# Revit family: Haworth_JiveTable_Rectangle_Legs
name_source: partatom
category: Furniture Systems
revit_build: Autodesk Revit 2018 (Build: 20170223_1515(x64)
units: mm (PartAtom-declared; Revit-internal decimal feet)

## family parameters
Always vertical = Yes
Cut with Voids When Loaded = No
OmniClass Number = 23.40.70.14.64.21
OmniClass Title = Systems Furniture
Part Type = Normal
Room Calculation Point = No
Round Connector Dimension = Use Diameter
Shared = No
Work Plane-Based = No

## types (268) — shared parameters
Assembly Code = E2020200
Custom Size = No
Leg Length = 14 141/256"
Manufacturer = Haworth, Inc.
Max. Depth = 60"
Max. Height = 42"
Max. Width = 84"
Min. Depth = 18"
Min. Height = 16"
Min. Width = 24"
Model = Hawoth Jive
Revision Number = 0
Size = Verify Final Dim. w/ Haworth
Standard Depths = 18, 24, 30, 36, 42, 48, 54, 60 in.
Standard Height = 16, 20, 29, 36, 42 in.
Standard Widths = 24, 30, 36, 42, 48, 54, 60, 66, 72, 84 in.
Table Thickness = 1 3/16"
URL = http://www.haworth.com
URL - Product = http://www.haworth.com
Warranty = http://www.haworth.com

## per-type parameters (varying)
| type | Actual Casters | Actual Depth | Actual Height | Actual Width | C Leg Extruded | C Leg Round | Casters | Depth | Description | Glides | Height | Leg Distance | Leg Height | Leg Spacing | Post Extruded Leg | Post Leg Spacing | Post Round Leg | T Leg Extruded | T Leg Round | Width |
| 30d 30w 29h - Post Extruded Base - With Casters | Yes | 30" | 29" | 30" | No | No | Yes | 30" | Haworth Jive Table Square Legs - 30d 30w 29h - Post Extruded Base - With Casters | No | 29" | 4 1/256" | 27 13/16" | 10 255/256" | Yes | 21 127/128" | No | No | No | 30" |
| 36d 36w 29h - Post Extruded Base - With Casters | Yes | 36" | 29" | 36" | No | No | Yes | 36" | Haworth Jive Table Square Legs - 36d 36w 29h - Post Extruded Base - With Casters | No | 29" | 4 1/256" | 27 13/16" | 13 255/256" | Yes | 27 127/128" | No | No | No | 36" |
| 42d 42w 29h - Post Extruded Base - With Casters | Yes | 42" | 29" | 42" | No | No | Yes | 42" | Haworth Jive Table Square Legs - 42d 42w 29h - Post Extruded Base - With Casters | No | 29" | 4 1/256" | 27 13/16" | 16 255/256" | Yes | 33 127/128" | No | No | No | 42" |
| 48d 48w 29h - Post Extruded Base - With Casters | Yes | 48" | 29" | 48" | No | No | Yes | 48" | Haworth Jive Table Square Legs - 48d 48w 29h - Post Extruded Base - With Casters | No | 29" | 4 1/256" | 27 13/16" | 19 255/256" | Yes | 39 127/128" | No | No | No | 48" |
| 54d 54w 29h - Post Extruded Base - With Casters | Yes | 54" | 29" | 54" | No | No | Yes | 54" | Haworth Jive Table Square Legs - 54d 54w 29h - Post Extruded Base - With Casters | No | 29" | 4 1/256" | 27 13/16" | 22 255/256" | Yes | 45 127/128" | No | No | No | 54" |
| 60d 60w 29h - Post Extruded Base - With Casters | Yes | 60" | 29" | 60" | No | No | Yes | 60" | Haworth Jive Table Square Legs - 60d 60w 29h - Post Extruded Base - With Casters | No | 29" | 4 1/256" | 27 13/16" | 25 255/256" | Yes | 51 127/128" | No | No | No | 60" |
| 24d 24w 16h - Post Extruded Base - With Glides | No | 24" | 16" | 24" | No | No | No | 24" | Haworth Jive Table Square Legs - 24d 24w 16h - Post Extruded Base - With Glides | Yes | 16" | 4 1/256" | 14 13/16" | 7 255/256" | Yes | 15 127/128" | No | No | No | 24" |
| 36d 36w 16h - Post Extruded Base - With Glides | No | 36" | 16" | 36" | No | No | No | 36" | Haworth Jive Table Square Legs - 36d 36w 16h - Post Extruded Base - With Glides | Yes | 16" | 4 1/256" | 14 13/16" | 13 255/256" | Yes | 27 127/128" | No | No | No | 36" |
| 42d 42w 16h - Post Extruded Base - With Glides | No | 42" | 16" | 42" | No | No | No | 42" | Haworth Jive Table Square Legs - 42d 42w 16h - Post Extruded Base - With Glides | Yes | 16" | 4 1/256" | 14 13/16" | 16 255/256" | Yes | 33 127/128" | No | No | No | 42" |
| 48d 48w 16h - Post Extruded Base - With Glides | No | 48" | 16" | 48" | No | No | No | 48" | Haworth Jive Table Square Legs - 48d 48w 16h - Post Extruded Base - With Glides | Yes | 16" | 4 1/256" | 14 13/16" | 19 255/256" | Yes | 39 127/128" | No | No | No | 48" |
| 24d 24w 20h - Post Extruded Base - With Glides | No | 24" | 20" | 24" | No | No | No | 24" | Haworth Jive Table Square Legs - 24d 24w 20h - Post Extruded Base - With Glides | Yes | 20" | 4 1/256" | 18 13/16" | 7 255/256" | Yes | 15 127/128" | No | No | No | 24" |
| 36d 36w 20h - Post Extruded Base - With Glides | No | 36" | 20" | 36" | No | No | No | 36" | Haworth Jive Table Square Legs - 36d 36w 20h - Post Extruded Base - With Glides | Yes | 20" | 4 1/256" | 18 13/16" | 13 255/256" | Yes | 27 127/128" | No | No | No | 36" |
| 42d 42w 20h - Post Extruded Base - With Glides | No | 42" | 20" | 42" | No | No | No | 42" | Haworth Jive Table Square Legs - 42d 42w 20h - Post Extruded Base - With Glides | Yes | 20" | 4 1/256" | 18 13/16" | 16 255/256" | Yes | 33 127/128" | No | No | No | 42" |
| 48d 48w 20h - Post Extruded Base - With Glides | No | 48" | 20" | 48" | No | No | No | 48" | Haworth Jive Table Square Legs - 48d 48w 20h - Post Extruded Base - With Glides | Yes | 20" | 4 1/256" | 18 13/16" | 19 255/256" | Yes | 39 127/128" | No | No | No | 48" |
| 30d 30w 29h - Post Extruded Base - With Glides | No | 30" | 29" | 30" | No | No | No | 30" | Haworth Jive Table Square Legs - 30d 30w 29h - Post Extruded Base - With Glides | Yes | 29" | 4 1/256" | 27 13/16" | 10 255/256" | Yes | 21 127/128" | No | No | No | 30" |
| 36d 36w 29h - Post Extruded Base - With Glides | No | 36" | 29" | 36" | No | No | No | 36" | Haworth Jive Table Square Legs - 36d 36w 29h - Post Extruded Base - With Glides | Yes | 29" | 4 1/256" | 27 13/16" | 13 255/256" | Yes | 27 127/128" | No | No | No | 36" |
| 42d 42w 29h - Post Extruded Base - With Glides | No | 42" | 29" | 42" | No | No | No | 42" | Haworth Jive Table Square Legs - 42d 42w 29h - Post Extruded Base - With Glides | Yes | 29" | 4 1/256" | 27 13/16" | 16 255/256" | Yes | 33 127/128" | No | No | No | 42" |
| 48d 48w 29h - Post Extruded Base - With Glides | No | 48" | 29" | 48" | No | No | No | 48" | Haworth Jive Table Square Legs - 48d 48w 29h - Post Extruded Base - With Glides | Yes | 29" | 4 1/256" | 27 13/16" | 19 255/256" | Yes | 39 127/128" | No | No | No | 48" |
| 54d 54w 29h - Post Extruded Base - With Glides | No | 54" | 29" | 54" | No | No | No | 54" | Haworth Jive Table Square Legs - 54d 54w 29h - Post Extruded Base - With Glides | Yes | 29" | 4 1/256" | 27 13/16" | 22 255/256" | Yes | 45 127/128" | No | No | No | 54" |
| 60d 60w 29h - Post Extruded Base - With Glides | No | 60" | 29" | 60" | No | No | No | 60" | Haworth Jive Table Square Legs - 60d 60w 29h - Post Extruded Base - With Glides | Yes | 29" | 4 1/256" | 27 13/16" | 25 255/256" | Yes | 51 127/128" | No | No | No | 60" |
| 18d 48w 29h - Post Extruded Base - With Casters | Yes | 18" | 29" | 48" | No | No | Yes | 18" | Haworth Jive Table Rectangle Legs - 18d 48w 29h - Post Extruded Base - With Casters | No | 29" | 4 1/256" | 27 13/16" | 4 255/256" | Yes | 9 127/128" | No | No | No | 48" |
| 18d 54w 29h - Post Extruded Base - With Casters | Yes | 18" | 29" | 54" | No | No | Yes | 18" | Haworth Jive Table Rectangle Legs - 18d 54w 29h - Post Extruded Base - With Casters | No | 29" | 4 1/256" | 27 13/16" | 4 255/256" | Yes | 9 127/128" | No | No | No | 54" |
| 18d 60w 29h - Post Extruded Base - With Casters | Yes | 18" | 29" | 60" | No | No | Yes | 18" | Haworth Jive Table Rectangle Legs - 18d 60w 29h - Post Extruded Base - With Casters | No | 29" | 4 1/256" | 27 13/16" | 4 255/256" | Yes | 9 127/128" | No | No | No | 60" |
| 18d 66w 29h - Post Extruded Base - With Casters | Yes | 18" | 29" | 66" | No | No | Yes | 18" | Haworth Jive Table Rectangle Legs - 18d 66w 29h - Post Extruded Base - With Casters | No | 29" | 4 1/256" | 27 13/16" | 4 255/256" | Yes | 9 127/128" | No | No | No | 66" |
| 18d 72w 29h - Post Extruded Base - With Casters | Yes | 18" | 29" | 72" | No | No | Yes | 18" | Haworth Jive Table Rectangle Legs - 18d 72w 29h - Post Extruded Base - With Casters | No | 29" | 4 1/256" | 27 13/16" | 4 255/256" | Yes | 9 127/128" | No | No | No | 72" |
| 24d 36w 29h - Post Extruded Base - With Casters | Yes | 24" | 29" | 36" | No | No | Yes | 24" | Haworth Jive Table Rectangle Legs - 24d 36w 29h - Post Extruded Base - With Casters | No | 29" | 4 1/256" | 27 13/16" | 7 255/256" | Yes | 15 127/128" | No | No | No | 36" |
| 24d 42w 29h - Post Extruded Base - With Casters | Yes | 24" | 29" | 42" | No | No | Yes | 24" | Haworth Jive Table Rectangle Legs - 24d 42w 29h - Post Extruded Base - With Casters | No | 29" | 4 1/256" | 27 13/16" | 7 255/256" | Yes | 15 127/128" | No | No | No | 42" |
| 24d 48w 29h - Post Extruded Base - With Casters | Yes | 24" | 29" | 48" | No | No | Yes | 24" | Haworth Jive Table Rectangle Legs - 24d 48w 29h - Post Extruded Base - With Casters | No | 29" | 4 1/256" | 27 13/16" | 7 255/256" | Yes | 15 127/128" | No | No | No | 48" |
| 24d 54w 29h - Post Extruded Base - With Casters | Yes | 24" | 29" | 54" | No | No | Yes | 24" | Haworth Jive Table Rectangle Legs - 24d 54w 29h - Post Extruded Base - With Casters | No | 29" | 4 1/256" | 27 13/16" | 7 255/256" | Yes | 15 127/128" | No | No | No | 54" |
| 24d 60w 29h - Post Extruded Base - With Casters | Yes | 24" | 29" | 60" | No | No | Yes | 24" | Haworth Jive Table Rectangle Legs - 24d 60w 29h - Post Extruded Base - With Casters | No | 29" | 4 1/256" | 27 13/16" | 7 255/256" | Yes | 15 127/128" | No | No | No | 60" |
| 24d 66w 29h - Post Extruded Base - With Casters | Yes | 24" | 29" | 66" | No | No | Yes | 24" | Haworth Jive Table Rectangle Legs - 24d 66w 29h - Post Extruded Base - With Casters | No | 29" | 4 1/256" | 27 13/16" | 7 255/256" | Yes | 15 127/128" | No | No | No | 66" |
| 24d 72w 29h - Post Extruded Base - With Casters | Yes | 24" | 29" | 72" | No | No | Yes | 24" | Haworth Jive Table Rectangle Legs - 24d 72w 29h - Post Extruded Base - With Casters | No | 29" | 4 1/256" | 27 13/16" | 7 255/256" | Yes | 15 127/128" | No | No | No | 72" |
| 30d 36w 29h - Post Extruded Base - With Casters | Yes | 30" | 29" | 36" | No | No | Yes | 30" | Haworth Jive Table Rectangle Legs - 30d 36w 29h - Post Extruded Base - With Casters | No | 29" | 4 1/256" | 27 13/16" | 10 255/256" | Yes | 21 127/128" | No | No | No | 36" |
| 30d 42w 29h - Post Extruded Base - With Casters | Yes | 30" | 29" | 42" | No | No | Yes | 30" | Haworth Jive Table Rectangle Legs - 30d 42w 29h - Post Extruded Base - With Casters | No | 29" | 4 1/256" | 27 13/16" | 10 255/256" | Yes | 21 127/128" | No | No | No | 42" |
| 30d 48w 29h - Post Extruded Base - With Casters | Yes | 30" | 29" | 48" | No | No | Yes | 30" | Haworth Jive Table Rectangle Legs - 30d 48w 29h - Post Extruded Base - With Casters | No | 29" | 4 1/256" | 27 13/16" | 10 255/256" | Yes | 21 127/128" | No | No | No | 48" |
| 30d 60w 29h - Post Extruded Base - With Casters | Yes | 30" | 29" | 60" | No | No | Yes | 30" | Haworth Jive Table Rectangle Legs - 30d 60w 29h - Post Extruded Base - With Casters | No | 29" | 4 1/256" | 27 13/16" | 10 255/256" | Yes | 21 127/128" | No | No | No | 60" |
| 30d 72w 29h - Post Extruded Base - With Casters | Yes | 30" | 29" | 72" | No | No | Yes | 30" | Haworth Jive Table Rectangle Legs - 30d 72w 29h - Post Extruded Base - With Casters | No | 29" | 4 1/256" | 27 13/16" | 10 255/256" | Yes | 21 127/128" | No | No | No | 72" |
| 36d 60w 29h - Post Extruded Base - With Casters | Yes | 36" | 29" | 60" | No | No | Yes | 36" | Haworth Jive Table Rectangle Legs - 36d 60w 29h - Post Extruded Base - With Casters | No | 29" | 4 1/256" | 27 13/16" | 13 255/256" | Yes | 27 127/128" | No | No | No | 60" |
| 36d 66w 29h - Post Extruded Base - With Casters | Yes | 36" | 29" | 66" | No | No | Yes | 36" | Haworth Jive Table Rectangle Legs - 36d 66w 29h - Post Extruded Base - With Casters | No | 29" | 4 1/256" | 27 13/16" | 13 255/256" | Yes | 27 127/128" | No | No | No | 66" |
| 36d 72w 29h - Post Extruded Base - With Casters | Yes | 36" | 29" | 72" | No | No | Yes | 36" | Haworth Jive Table Rectangle Legs - 36d 72w 29h - Post Extruded Base - With Casters | No | 29" | 4 1/256" | 27 13/16" | 13 255/256" | Yes | 27 127/128" | No | No | No | 72" |
| 36d 84w 29h - Post Extruded Base - With Casters | Yes | 36" | 29" | 84" | No | No | Yes | 36" | Haworth Jive Table Rectangle Legs - 36d 84w 29h - Post Extruded Base - With Casters | No | 29" | 4 1/256" | 27 13/16" | 13 255/256" | Yes | 27 127/128" | No | No | No | 84" |
| 18d 48w 29h - Post Extruded Base - With Glides | No | 18" | 29" | 48" | No | No | No | 18" | Haworth Jive Table Rectangle Legs - 18d 48w 29h - Post Extruded Base - With Glides | Yes | 29" | 4 1/256" | 27 13/16" | 4 255/256" | Yes | 9 127/128" | No | No | No | 48" |
| 18d 54w 29h - Post Extruded Base - With Glides | No | 18" | 29" | 54" | No | No | No | 18" | Haworth Jive Table Rectangle Legs - 18d 54w 29h - Post Extruded Base - With Glides | Yes | 29" | 4 1/256" | 27 13/16" | 4 255/256" | Yes | 9 127/128" | No | No | No | 54" |
| 18d 60w 29h - Post Extruded Base - With Glides | No | 18" | 29" | 60" | No | No | No | 18" | Haworth Jive Table Rectangle Legs - 18d 60w 29h - Post Extruded Base - With Glides | Yes | 29" | 4 1/256" | 27 13/16" | 4 255/256" | Yes | 9 127/128" | No | No | No | 60" |
| 18d 66w 29h - Post Extruded Base - With Glides | No | 18" | 29" | 66" | No | No | No | 18" | Haworth Jive Table Rectangle Legs - 18d 66w 29h - Post Extruded Base - With Glides | Yes | 29" | 4 1/256" | 27 13/16" | 4 255/256" | Yes | 9 127/128" | No | No | No | 66" |
| 18d 72w 29h - Post Extruded Base - With Glides | No | 18" | 29" | 72" | No | No | No | 18" | Haworth Jive Table Rectangle Legs - 18d 72w 29h - Post Extruded Base - With Glides | Yes | 29" | 4 1/256" | 27 13/16" | 4 255/256" | Yes | 9 127/128" | No | No | No | 72" |
| 24d 36w 29h - Post Extruded Base - With Glides | No | 24" | 29" | 36" | No | No | No | 24" | Haworth Jive Table Rectangle Legs - 24d 36w 29h - Post Extruded Base - With Glides | Yes | 29" | 4 1/256" | 27 13/16" | 7 255/256" | Yes | 15 127/128" | No | No | No | 36" |
| 24d 42w 29h - Post Extruded Base - With Glides | No | 24" | 29" | 42" | No | No | No | 24" | Haworth Jive Table Rectangle Legs - 24d 42w 29h - Post Extruded Base - With Glides | Yes | 29" | 4 1/256" | 27 13/16" | 7 255/256" | Yes | 15 127/128" | No | No | No | 42" |
| 24d 48w 29h - Post Extruded Base - With Glides | No | 24" | 29" | 48" | No | No | No | 24" | Haworth Jive Table Rectangle Legs - 24d 48w 29h - Post Extruded Base - With Glides | Yes | 29" | 4 1/256" | 27 13/16" | 7 255/256" | Yes | 15 127/128" | No | No | No | 48" |
| 24d 54w 29h - Post Extruded Base - With Glides | No | 24" | 29" | 54" | No | No | No | 24" | Haworth Jive Table Rectangle Legs - 24d 54w 29h - Post Extruded Base - With Glides | Yes | 29" | 4 1/256" | 27 13/16" | 7 255/256" | Yes | 15 127/128" | No | No | No | 54" |
| 24d 60w 29h - Post Extruded Base - With Glides | No | 24" | 29" | 60" | No | No | No | 24" | Haworth Jive Table Rectangle Legs - 24d 60w 29h - Post Extruded Base - With Glides | Yes | 29" | 4 1/256" | 27 13/16" | 7 255/256" | Yes | 15 127/128" | No | No | No | 60" |
| 24d 66w 29h - Post Extruded Base - With Glides | No | 24" | 29" | 66" | No | No | No | 24" | Haworth Jive Table Rectangle Legs - 24d 66w 29h - Post Extruded Base - With Glides | Yes | 29" | 4 1/256" | 27 13/16" | 7 255/256" | Yes | 15 127/128" | No | No | No | 66" |
| 24d 72w 29h - Post Extruded Base - With Glides | No | 24" | 29" | 72" | No | No | No | 24" | Haworth Jive Table Rectangle Legs - 24d 72w 29h - Post Extruded Base - With Glides | Yes | 29" | 4 1/256" | 27 13/16" | 7 255/256" | Yes | 15 127/128" | No | No | No | 72" |
| 30d 36w 29h - Post Extruded Base - With Glides | No | 30" | 29" | 36" | No | No | No | 30" | Haworth Jive Table Rectangle Legs - 30d 36w 29h - Post Extruded Base - With Glides | Yes | 29" | 4 1/256" | 27 13/16" | 10 255/256" | Yes | 21 127/128" | No | No | No | 36" |
| 30d 42w 29h - Post Extruded Base - With Glides | No | 30" | 29" | 42" | No | No | No | 30" | Haworth Jive Table Rectangle Legs - 30d 42w 29h - Post Extruded Base - With Glides | Yes | 29" | 4 1/256" | 27 13/16" | 10 255/256" | Yes | 21 127/128" | No | No | No | 42" |
| 30d 48w 29h - Post Extruded Base - With Glides | No | 30" | 29" | 48" | No | No | No | 30" | Haworth Jive Table Rectangle Legs - 30d 48w 29h - Post Extruded Base - With Glides | Yes | 29" | 4 1/256" | 27 13/16" | 10 255/256" | Yes | 21 127/128" | No | No | No | 48" |
| 30d 60w 29h - Post Extruded Base - With Glides | No | 30" | 29" | 60" | No | No | No | 30" | Haworth Jive Table Rectangle Legs - 30d 60w 29h - Post Extruded Base - With Glides | Yes | 29" | 4 1/256" | 27 13/16" | 10 255/256" | Yes | 21 127/128" | No | No | No | 60" |
| 30d 72w 29h - Post Extruded Base - With Glides | No | 30" | 29" | 72" | No | No | No | 30" | Haworth Jive Table Rectangle Legs - 30d 72w 29h - Post Extruded Base - With Glides | Yes | 29" | 4 1/256" | 27 13/16" | 10 255/256" | Yes | 21 127/128" | No | No | No | 72" |
| 36d 60w 29h - Post Extruded Base - With Glides | No | 36" | 29" | 60" | No | No | No | 36" | Haworth Jive Table Rectangle Legs - 36d 60w 29h - Post Extruded Base - With Glides | Yes | 29" | 4 1/256" | 27 13/16" | 13 255/256" | Yes | 27 127/128" | No | No | No | 60" |
| 36d 66w 29h - Post Extruded Base - With Glides | No | 36" | 29" | 66" | No | No | No | 36" | Haworth Jive Table Rectangle Legs - 36d 66w 29h - Post Extruded Base - With Glides | Yes | 29" | 4 1/256" | 27 13/16" | 13 255/256" | Yes | 27 127/128" | No | No | No | 66" |
| 36d 72w 29h - Post Extruded Base - With Glides | No | 36" | 29" | 72" | No | No | No | 36" | Haworth Jive Table Rectangle Legs - 36d 72w 29h - Post Extruded Base - With Glides | Yes | 29" | 4 1/256" | 27 13/16" | 13 255/256" | Yes | 27 127/128" | No | No | No | 72" |
| 36d 84w 29h - Post Extruded Base - With Glides | No | 36" | 29" | 84" | No | No | No | 36" | Haworth Jive Table Rectangle Legs - 36d 84w 29h - Post Extruded Base - With Glides | Yes | 29" | 4 1/256" | 27 13/16" | 13 255/256" | Yes | 27 127/128" | No | No | No | 84" |
| 30d 30w 29h - Post Round Base - With Casters | Yes | 30" | 29" | 30" | No | No | Yes | 30" | Haworth Jive Table Square Legs - 30d 30w 29h - Post Round Base - With Casters | No | 29" | 4 1/256" | 27 13/16" | 10 255/256" | No | 21 127/128" | Yes | No | No | 30" |
| 36d 36w 29h - Post Round Base - With Casters | Yes | 36" | 29" | 36" | No | No | Yes | 36" | Haworth Jive Table Square Legs - 36d 36w 29h - Post Round Base - With Casters | No | 29" | 4 1/256" | 27 13/16" | 13 255/256" | No | 27 127/128" | Yes | No | No | 36" |
| 42d 42w 29h - Post Round Base - With Casters | Yes | 42" | 29" | 42" | No | No | Yes | 42" | Haworth Jive Table Square Legs - 42d 42w 29h - Post Round Base - With Casters | No | 29" | 4 1/256" | 27 13/16" | 16 255/256" | No | 33 127/128" | Yes | No | No | 42" |
| 48d 48w 29h - Post Round Base - With Casters | Yes | 48" | 29" | 48" | No | No | Yes | 48" | Haworth Jive Table Square Legs - 48d 48w 29h - Post Round Base - With Casters | No | 29" | 4 1/256" | 27 13/16" | 19 255/256" | No | 39 127/128" | Yes | No | No | 48" |
| 30d 30w 29h - Post Round Base - With Glides | No | 30" | 29" | 30" | No | No | No | 30" | Haworth Jive Table Square Legs - 30d 30w 29h - Post Round Base - With Glides | Yes | 29" | 4 1/256" | 27 13/16" | 10 255/256" | No | 21 127/128" | Yes | No | No | 30" |
| 36d 36w 29h - Post Round Base - With Glides | No | 36" | 29" | 36" | No | No | No | 36" | Haworth Jive Table Square Legs - 36d 36w 29h - Post Round Base - With Glides | Yes | 29" | 4 1/256" | 27 13/16" | 13 255/256" | No | 27 127/128" | Yes | No | No | 36" |
| 42d 42w 29h - Post Round Base - With Glides | No | 42" | 29" | 42" | No | No | No | 42" | Haworth Jive Table Square Legs - 42d 42w 29h - Post Round Base - With Glides | Yes | 29" | 4 1/256" | 27 13/16" | 16 255/256" | No | 33 127/128" | Yes | No | No | 42" |
| 48d 48w 29h - Post Round Base - With Glides | No | 48" | 29" | 48" | No | No | No | 48" | Haworth Jive Table Square Legs - 48d 48w 29h - Post Round Base - With Glides | Yes | 29" | 4 1/256" | 27 13/16" | 19 255/256" | No | 39 127/128" | Yes | No | No | 48" |
| 18d 48w 29h - Post Round Base - With Casters | Yes | 18" | 29" | 48" | No | No | Yes | 18" | Haworth Jive Table Rectangle Legs - 18d 48w 29h - Post Round Base - With Casters | No | 29" | 4 1/256" | 27 13/16" | 4 255/256" | No | 9 127/128" | Yes | No | No | 48" |
| 18d 54w 29h - Post Round Base - With Casters | Yes | 18" | 29" | 54" | No | No | Yes | 18" | Haworth Jive Table Rectangle Legs - 18d 54w 29h - Post Round Base - With Casters | No | 29" | 4 1/256" | 27 13/16" | 4 255/256" | No | 9 127/128" | Yes | No | No | 54" |
| 18d 60w 29h - Post Round Base - With Casters | Yes | 18" | 29" | 60" | No | No | Yes | 18" | Haworth Jive Table Rectangle Legs - 18d 60w 29h - Post Round Base - With Casters | No | 29" | 4 1/256" | 27 13/16" | 4 255/256" | No | 9 127/128" | Yes | No | No | 60" |
| 18d 66w 29h - Post Round Base - With Casters | Yes | 18" | 29" | 66" | No | No | Yes | 18" | Haworth Jive Table Rectangle Legs - 18d 66w 29h - Post Round Base - With Casters | No | 29" | 4 1/256" | 27 13/16" | 4 255/256" | No | 9 127/128" | Yes | No | No | 66" |
| 18d 72w 29h - Post Round Base - With Casters | Yes | 18" | 29" | 72" | No | No | Yes | 18" | Haworth Jive Table Rectangle Legs - 18d 72w 29h - Post Round Base - With Casters | No | 29" | 4 1/256" | 27 13/16" | 4 255/256" | No | 9 127/128" | Yes | No | No | 72" |
| 24d 36w 29h - Post Round Base - With Casters | Yes | 24" | 29" | 36" | No | No | Yes | 24" | Haworth Jive Table Rectangle Legs - 24d 36w 29h - Post Round Base - With Casters | No | 29" | 4 1/256" | 27 13/16" | 7 255/256" | No | 15 127/128" | Yes | No | No | 36" |
| 24d 42w 29h - Post Round Base - With Casters | Yes | 24" | 29" | 42" | No | No | Yes | 24" | Haworth Jive Table Rectangle Legs - 24d 42w 29h - Post Round Base - With Casters | No | 29" | 4 1/256" | 27 13/16" | 7 255/256" | No | 15 127/128" | Yes | No | No | 42" |
| 24d 48w 29h - Post Round Base - With Casters | Yes | 24" | 29" | 48" | No | No | Yes | 24" | Haworth Jive Table Rectangle Legs - 24d 48w 29h - Post Round Base - With Casters | No | 29" | 4 1/256" | 27 13/16" | 7 255/256" | No | 15 127/128" | Yes | No | No | 48" |
| 24d 54w 29h - Post Round Base - With Casters | Yes | 24" | 29" | 54" | No | No | Yes | 24" | Haworth Jive Table Rectangle Legs - 24d 54w 29h - Post Round Base - With Casters | No | 29" | 4 1/256" | 27 13/16" | 7 255/256" | No | 15 127/128" | Yes | No | No | 54" |
| 24d 60w 29h - Post Round Base - With Casters | Yes | 24" | 29" | 60" | No | No | Yes | 24" | Haworth Jive Table Rectangle Legs - 24d 60w 29h - Post Round Base - With Casters | No | 29" | 4 1/256" | 27 13/16" | 7 255/256" | No | 15 127/128" | Yes | No | No | 60" |
| 24d 66w 29h - Post Round Base - With Casters | Yes | 24" | 29" | 66" | No | No | Yes | 24" | Haworth Jive Table Rectangle Legs - 24d 66w 29h - Post Round Base - With Casters | No | 29" | 4 1/256" | 27 13/16" | 7 255/256" | No | 15 127/128" | Yes | No | No | 66" |
| 24d 72w 29h - Post Round Base - With Casters | Yes | 24" | 29" | 72" | No | No | Yes | 24" | Haworth Jive Table Rectangle Legs - 24d 72w 29h - Post Round Base - With Casters | No | 29" | 4 1/256" | 27 13/16" | 7 255/256" | No | 15 127/128" | Yes | No | No | 72" |
| 30d 36w 29h - Post Round Base - With Casters | Yes | 30" | 29" | 36" | No | No | Yes | 30" | Haworth Jive Table Rectangle Legs - 30d 36w 29h - Post Round Base - With Casters | No | 29" | 4 1/256" | 27 13/16" | 10 255/256" | No | 21 127/128" | Yes | No | No | 36" |
| 30d 42w 29h - Post Round Base - With Casters | Yes | 30" | 29" | 42" | No | No | Yes | 30" | Haworth Jive Table Rectangle Legs - 30d 42w 29h - Post Round Base - With Casters | No | 29" | 4 1/256" | 27 13/16" | 10 255/256" | No | 21 127/128" | Yes | No | No | 42" |
| 30d 48w 29h - Post Round Base - With Casters | Yes | 30" | 29" | 48" | No | No | Yes | 30" | Haworth Jive Table Rectangle Legs - 30d 48w 29h - Post Round Base - With Casters | No | 29" | 4 1/256" | 27 13/16" | 10 255/256" | No | 21 127/128" | Yes | No | No | 48" |
| 30d 54w 29h - Post Round Base - With Casters | Yes | 30" | 29" | 54" | No | No | Yes | 30" | Haworth Jive Table Rectangle Legs - 30d 54w 29h - Post Round Base - With Casters | No | 29" | 4 1/256" | 27 13/16" | 10 255/256" | No | 21 127/128" | Yes | No | No | 54" |
| 30d 60w 29h - Post Round Base - With Casters | Yes | 30" | 29" | 60" | No | No | Yes | 30" | Haworth Jive Table Rectangle Legs - 30d 60w 29h - Post Round Base - With Casters | No | 29" | 4 1/256" | 27 13/16" | 10 255/256" | No | 21 127/128" | Yes | No | No | 60" |
| 30d 72w 29h - Post Round Base - With Casters | Yes | 30" | 29" | 72" | No | No | Yes | 30" | Haworth Jive Table Rectangle Legs - 30d 72w 29h - Post Round Base - With Casters | No | 29" | 4 1/256" | 27 13/16" | 10 255/256" | No | 21 127/128" | Yes | No | No | 72" |
| 36d 60w 29h - Post Round Base - With Casters | Yes | 36" | 29" | 60" | No | No | Yes | 36" | Haworth Jive Table Rectangle Legs - 36d 60w 29h - Post Round Base - With Casters | No | 29" | 4 1/256" | 27 13/16" | 13 255/256" | No | 27 127/128" | Yes | No | No | 60" |
| 36d 66w 29h - Post Round Base - With Casters | Yes | 36" | 29" | 66" | No | No | Yes | 36" | Haworth Jive Table Rectangle Legs - 36d 66w 29h - Post Round Base - With Casters | No | 29" | 4 1/256" | 27 13/16" | 13 255/256" | No | 27 127/128" | Yes | No | No | 66" |
| 36d 72w 29h - Post Round Base - With Casters | Yes | 36" | 29" | 72" | No | No | Yes | 36" | Haworth Jive Table Rectangle Legs - 36d 72w 29h - Post Round Base - With Casters | No | 29" | 4 1/256" | 27 13/16" | 13 255/256" | No | 27 127/128" | Yes | No | No | 72" |
| 18d 48w 29h - Post Round Base - With Glides | No | 18" | 29" | 48" | No | No | No | 18" | Haworth Jive Table Rectangle Legs - 18d 48w 29h - Post Round Base - With Glides | Yes | 29" | 4 1/256" | 27 13/16" | 4 255/256" | No | 9 127/128" | Yes | No | No | 48" |
| 18d 54w 29h - Post Round Base - With Glides | No | 18" | 29" | 54" | No | No | No | 18" | Haworth Jive Table Rectangle Legs - 18d 54w 29h - Post Round Base - With Glides | Yes | 29" | 4 1/256" | 27 13/16" | 4 255/256" | No | 9 127/128" | Yes | No | No | 54" |
| 18d 60w 29h - Post Round Base - With Glides | No | 18" | 29" | 60" | No | No | No | 18" | Haworth Jive Table Rectangle Legs - 18d 60w 29h - Post Round Base - With Glides | Yes | 29" | 4 1/256" | 27 13/16" | 4 255/256" | No | 9 127/128" | Yes | No | No | 60" |
| 18d 66w 29h - Post Round Base - With Glides | No | 18" | 29" | 66" | No | No | No | 18" | Haworth Jive Table Rectangle Legs - 18d 66w 29h - Post Round Base - With Glides | Yes | 29" | 4 1/256" | 27 13/16" | 4 255/256" | No | 9 127/128" | Yes | No | No | 66" |
| 18d 72w 29h - Post Round Base - With Glides | No | 18" | 29" | 72" | No | No | No | 18" | Haworth Jive Table Rectangle Legs - 18d 72w 29h - Post Round Base - With Glides | Yes | 29" | 4 1/256" | 27 13/16" | 4 255/256" | No | 9 127/128" | Yes | No | No | 72" |
| 24d 36w 29h - Post Round Base - With Glides | No | 24" | 29" | 36" | No | No | No | 24" | Haworth Jive Table Rectangle Legs - 24d 36w 29h - Post Round Base - With Glides | Yes | 29" | 4 1/256" | 27 13/16" | 7 255/256" | No | 15 127/128" | Yes | No | No | 36" |
| 24d 42w 29h - Post Round Base - With Glides | No | 24" | 29" | 42" | No | No | No | 24" | Haworth Jive Table Rectangle Legs - 24d 42w 29h - Post Round Base - With Glides | Yes | 29" | 4 1/256" | 27 13/16" | 7 255/256" | No | 15 127/128" | Yes | No | No | 42" |
| 24d 48w 29h - Post Round Base - With Glides | No | 24" | 29" | 48" | No | No | No | 24" | Haworth Jive Table Rectangle Legs - 24d 48w 29h - Post Round Base - With Glides | Yes | 29" | 4 1/256" | 27 13/16" | 7 255/256" | No | 15 127/128" | Yes | No | No | 48" |
| 24d 54w 29h - Post Round Base - With Glides | No | 24" | 29" | 54" | No | No | No | 24" | Haworth Jive Table Rectangle Legs - 24d 54w 29h - Post Round Base - With Glides | Yes | 29" | 4 1/256" | 27 13/16" | 7 255/256" | No | 15 127/128" | Yes | No | No | 54" |
| 24d 60w 29h - Post Round Base - With Glides | No | 24" | 29" | 60" | No | No | No | 24" | Haworth Jive Table Rectangle Legs - 24d 60w 29h - Post Round Base - With Glides | Yes | 29" | 4 1/256" | 27 13/16" | 7 255/256" | No | 15 127/128" | Yes | No | No | 60" |
| 24d 66w 29h - Post Round Base - With Glides | No | 24" | 29" | 66" | No | No | No | 24" | Haworth Jive Table Rectangle Legs - 24d 66w 29h - Post Round Base - With Glides | Yes | 29" | 4 1/256" | 27 13/16" | 7 255/256" | No | 15 127/128" | Yes | No | No | 66" |
| 24d 72w 29h - Post Round Base - With Glides | No | 24" | 29" | 72" | No | No | No | 24" | Haworth Jive Table Rectangle Legs - 24d 72w 29h - Post Round Base - With Glides | Yes | 29" | 4 1/256" | 27 13/16" | 7 255/256" | No | 15 127/128" | Yes | No | No | 72" |
| 30d 36w 29h - Post Round Base - With Glides | No | 30" | 29" | 36" | No | No | No | 30" | Haworth Jive Table Rectangle Legs - 30d 36w 29h - Post Round Base - With Glides | Yes | 29" | 4 1/256" | 27 13/16" | 10 255/256" | No | 21 127/128" | Yes | No | No | 36" |
| 30d 42w 29h - Post Round Base - With Glides | No | 30" | 29" | 42" | No | No | No | 30" | Haworth Jive Table Rectangle Legs - 30d 42w 29h - Post Round Base - With Glides | Yes | 29" | 4 1/256" | 27 13/16" | 10 255/256" | No | 21 127/128" | Yes | No | No | 42" |
| 30d 48w 29h - Post Round Base - With Glides | No | 30" | 29" | 48" | No | No | No | 30" | Haworth Jive Table Rectangle Legs - 30d 48w 29h - Post Round Base - With Glides | Yes | 29" | 4 1/256" | 27 13/16" | 10 255/256" | No | 21 127/128" | Yes | No | No | 48" |
| 30d 54w 29h - Post Round Base - With Glides | No | 30" | 29" | 54" | No | No | No | 30" | Haworth Jive Table Rectangle Legs - 30d 54w 29h - Post Round Base - With Glides | Yes | 29" | 4 1/256" | 27 13/16" | 10 255/256" | No | 21 127/128" | Yes | No | No | 54" |
| 30d 60w 29h - Post Round Base - With Glides | No | 30" | 29" | 60" | No | No | No | 30" | Haworth Jive Table Rectangle Legs - 30d 60w 29h - Post Round Base - With Glides | Yes | 29" | 4 1/256" | 27 13/16" | 10 255/256" | No | 21 127/128" | Yes | No | No | 60" |
| 30d 72w 29h - Post Round Base - With Glides | No | 30" | 29" | 72" | No | No | No | 30" | Haworth Jive Table Rectangle Legs - 30d 72w 29h - Post Round Base - With Glides | Yes | 29" | 4 1/256" | 27 13/16" | 10 255/256" | No | 21 127/128" | Yes | No | No | 72" |
| 36d 60w 29h - Post Round Base - With Glides | No | 36" | 29" | 60" | No | No | No | 36" | Haworth Jive Table Rectangle Legs - 36d 60w 29h - Post Round Base - With Glides | Yes | 29" | 4 1/256" | 27 13/16" | 13 255/256" | No | 27 127/128" | Yes | No | No | 60" |
| 36d 66w 29h - Post Round Base - With Glides | No | 36" | 29" | 66" | No | No | No | 36" | Haworth Jive Table Rectangle Legs - 36d 66w 29h - Post Round Base - With Glides | Yes | 29" | 4 1/256" | 27 13/16" | 13 255/256" | No | 27 127/128" | Yes | No | No | 66" |
| 36d 72w 29h - Post Round Base - With Glides | No | 36" | 29" | 72" | No | No | No | 36" | Haworth Jive Table Rectangle Legs - 36d 72w 29h - Post Round Base - With Glides | Yes | 29" | 4 1/256" | 27 13/16" | 13 255/256" | No | 27 127/128" | Yes | No | No | 72" |
| 24d 36w 29h - C Leg Extruded - With Casters | Yes | 24" | 29" | 36" | Yes | No | Yes | 24" | Haworth Jive Table Rectangle Legs - 24d 36w 29h - C Leg Extruded - With Casters | No | 29" | 7 91/128" | 27 13/16" | 4 37/128" | No | 15 127/128" | No | No | No | 36" |
| 24d 42w 29h - C Leg Extruded - With Casters | Yes | 24" | 29" | 42" | Yes | No | Yes | 24" | Haworth Jive Table Rectangle Legs - 24d 42w 29h - C Leg Extruded - With Casters | No | 29" | 7 91/128" | 27 13/16" | 4 37/128" | No | 15 127/128" | No | No | No | 42" |
| 24d 48w 29h - C Leg Extruded - With Casters | Yes | 24" | 29" | 48" | Yes | No | Yes | 24" | Haworth Jive Table Rectangle Legs - 24d 48w 29h - C Leg Extruded - With Casters | No | 29" | 7 91/128" | 27 13/16" | 4 37/128" | No | 15 127/128" | No | No | No | 48" |
| 24d 54w 29h - C Leg Extruded- With Casters | Yes | 24" | 29" | 54" | Yes | No | Yes | 24" | Haworth Jive Table Rectangle Legs - 24d 54w 29h - C Leg Extruded- With Casters | No | 29" | 7 91/128" | 27 13/16" | 4 37/128" | No | 15 127/128" | No | No | No | 54" |
| 24d 60w 29h - C Leg Extruded - With Casters | Yes | 24" | 29" | 60" | Yes | No | Yes | 24" | Haworth Jive Table Rectangle Legs - 24d 60w 29h - C Leg Extruded - With Casters | No | 29" | 7 91/128" | 27 13/16" | 4 37/128" | No | 15 127/128" | No | No | No | 60" |
| 24d 66w 29h - C Leg Extruded - With Casters | Yes | 24" | 29" | 66" | Yes | No | Yes | 24" | Haworth Jive Table Rectangle Legs - 24d 66w 29h - C Leg Extruded - With Casters | No | 29" | 7 91/128" | 27 13/16" | 4 37/128" | No | 15 127/128" | No | No | No | 66" |
| 24d 72w 29h - C Leg Extruded - With Casters | Yes | 24" | 29" | 72" | Yes | No | Yes | 24" | Haworth Jive Table Rectangle Legs - 24d 72w 29h - C Leg Extruded - With Casters | No | 29" | 7 91/128" | 27 13/16" | 4 37/128" | No | 15 127/128" | No | No | No | 72" |
| 30d 36w 29h - C Leg Extruded - With Casters | Yes | 30" | 29" | 36" | Yes | No | Yes | 30" | Haworth Jive Table Rectangle Legs - 30d 36w 29h - C Leg Extruded - With Casters | No | 29" | 7 91/128" | 27 13/16" | 7 37/128" | No | 21 127/128" | No | No | No | 36" |
| 30d 42w 29h - C Leg Extruded - With Casters | Yes | 30" | 29" | 42" | Yes | No | Yes | 30" | Haworth Jive Table Rectangle Legs - 30d 42w 29h - C Leg Extruded - With Casters | No | 29" | 7 91/128" | 27 13/16" | 7 37/128" | No | 21 127/128" | No | No | No | 42" |
| 30d 48w 29h - C Leg Extruded - With Casters | Yes | 30" | 29" | 48" | Yes | No | Yes | 30" | Haworth Jive Table Rectangle Legs - 30d 48w 29h - C Leg Extruded - With Casters | No | 29" | 7 91/128" | 27 13/16" | 7 37/128" | No | 21 127/128" | No | No | No | 48" |
| 30d 54w 29h - C Leg Extruded - With Casters | Yes | 30" | 29" | 54" | Yes | No | Yes | 30" | Haworth Jive Table Rectangle Legs - 30d 54w 29h - C Leg Extruded - With Casters | No | 29" | 7 91/128" | 27 13/16" | 7 37/128" | No | 21 127/128" | No | No | No | 54" |
| 30d 60w 29h - C Leg Extruded - With Casters | Yes | 30" | 29" | 60" | Yes | No | Yes | 30" | Haworth Jive Table Rectangle Legs - 30d 60w 29h - C Leg Extruded - With Casters | No | 29" | 7 91/128" | 27 13/16" | 7 37/128" | No | 21 127/128" | No | No | No | 60" |
| 30d 66w 29h - C Leg Extruded - With Casters | Yes | 30" | 29" | 66" | Yes | No | Yes | 30" | Haworth Jive Table Rectangle Legs - 30d 66w 29h - C Leg Extruded - With Casters | No | 29" | 7 91/128" | 27 13/16" | 7 37/128" | No | 21 127/128" | No | No | No | 66" |
| 30d 72w 29h - C Leg Extruded - With Casters | Yes | 30" | 29" | 72" | Yes | No | Yes | 30" | Haworth Jive Table Rectangle Legs - 30d 72w 29h - C Leg Extruded - With Casters | No | 29" | 7 91/128" | 27 13/16" | 7 37/128" | No | 21 127/128" | No | No | No | 72" |
| 24d 36w 29h - C Leg Extruded - With Glides | No | 24" | 29" | 36" | Yes | No | No | 24" | Haworth Jive Table Rectangle Legs - 24d 36w 29h - C Leg Extruded - With Glides | Yes | 29" | 7 91/128" | 27 13/16" | 4 37/128" | No | 15 127/128" | No | No | No | 36" |
| 24d 42w 29h - C Leg Extruded - With Glides | No | 24" | 29" | 42" | Yes | No | No | 24" | Haworth Jive Table Rectangle Legs - 24d 42w 29h - C Leg Extruded - With Glides | Yes | 29" | 7 91/128" | 27 13/16" | 4 37/128" | No | 15 127/128" | No | No | No | 42" |
| 24d 48w 29h - C Leg Extruded - With Glides | No | 24" | 29" | 48" | Yes | No | No | 24" | Haworth Jive Table Rectangle Legs - 24d 48w 29h - C Leg Extruded - With Glides | Yes | 29" | 7 91/128" | 27 13/16" | 4 37/128" | No | 15 127/128" | No | No | No | 48" |
| 24d 54w 29h - C Leg Extruded - With Glides | No | 24" | 29" | 54" | Yes | No | No | 24" | Haworth Jive Table Rectangle Legs - 24d 54w 29h - C Leg Extruded - With Glides | Yes | 29" | 7 91/128" | 27 13/16" | 4 37/128" | No | 15 127/128" | No | No | No | 54" |
| 24d 60w 29h - C Leg Extruded - With Glides | No | 24" | 29" | 60" | Yes | No | No | 24" | Haworth Jive Table Rectangle Legs - 24d 60w 29h - C Leg Extruded - With Glides | Yes | 29" | 7 91/128" | 27 13/16" | 4 37/128" | No | 15 127/128" | No | No | No | 60" |
| 24d 66w 29h - C Leg Extruded - With Glides | No | 24" | 29" | 66" | Yes | No | No | 24" | Haworth Jive Table Rectangle Legs - 24d 66w 29h - C Leg Extruded - With Glides | Yes | 29" | 7 91/128" | 27 13/16" | 4 37/128" | No | 15 127/128" | No | No | No | 66" |
| 24d 72w 29h - C Leg Extruded - With Glides | No | 24" | 29" | 72" | Yes | No | No | 24" | Haworth Jive Table Rectangle Legs - 24d 72w 29h - C Leg Extruded - With Glides | Yes | 29" | 7 91/128" | 27 13/16" | 4 37/128" | No | 15 127/128" | No | No | No | 72" |
| 30d 36w 29h - C Leg Extruded - With Glides | No | 30" | 29" | 36" | Yes | No | No | 30" | Haworth Jive Table Rectangle Legs - 30d 36w 29h - C Leg Extruded - With Glides | Yes | 29" | 7 91/128" | 27 13/16" | 7 37/128" | No | 21 127/128" | No | No | No | 36" |
| 30d 42w 29h - C Leg Extruded - With Glides | No | 30" | 29" | 42" | Yes | No | No | 30" | Haworth Jive Table Rectangle Legs - 30d 42w 29h - C Leg Extruded - With Glides | Yes | 29" | 7 91/128" | 27 13/16" | 7 37/128" | No | 21 127/128" | No | No | No | 42" |
| 30d 48w 29h - C Leg Extruded - With Glides | No | 30" | 29" | 48" | Yes | No | No | 30" | Haworth Jive Table Rectangle Legs - 30d 48w 29h - C Leg Extruded - With Glides | Yes | 29" | 7 91/128" | 27 13/16" | 7 37/128" | No | 21 127/128" | No | No | No | 48" |
| 30d 54w 29h - C Leg Extruded - With Glides | No | 30" | 29" | 54" | Yes | No | No | 30" | Haworth Jive Table Rectangle Legs - 30d 54w 29h - C Leg Extruded - With Glides | Yes | 29" | 7 91/128" | 27 13/16" | 7 37/128" | No | 21 127/128" | No | No | No | 54" |
| 30d 60w 29h - C Leg Extruded - With Glides | No | 30" | 29" | 60" | Yes | No | No | 30" | Haworth Jive Table Rectangle Legs - 30d 60w 29h - C Leg Extruded - With Glides | Yes | 29" | 7 91/128" | 27 13/16" | 7 37/128" | No | 21 127/128" | No | No | No | 60" |
| 30d 66w 29h - C Leg Extruded - With Glides | No | 30" | 29" | 66" | Yes | No | No | 30" | Haworth Jive Table Rectangle Legs - 30d 66w 29h - C Leg Extruded - With Glides | Yes | 29" | 7 91/128" | 27 13/16" | 7 37/128" | No | 21 127/128" | No | No | No | 66" |
| 30d 72w 29h - C Leg Extruded - With Glides | No | 30" | 29" | 72" | Yes | No | No | 30" | Haworth Jive Table Rectangle Legs - 30d 72w 29h - C Leg Extruded - With Glides | Yes | 29" | 7 91/128" | 27 13/16" | 7 37/128" | No | 21 127/128" | No | No | No | 72" |
| 24d 48w 42h - C Leg Extruded - With Glides | No | 24" | 42" | 48" | Yes | No | No | 24" | Haworth Jive Table Rectangle Legs - 24d 48w 42h - C Leg Extruded - With Glides | Yes | 42" | 7 91/128" | 40 13/16" | 4 37/128" | No | 15 127/128" | No | No | No | 48" |
| 24d 54w 42h - C Leg Extruded - With Glides | No | 24" | 42" | 54" | Yes | No | No | 24" | Haworth Jive Table Rectangle Legs - 24d 54w 42h - C Leg Extruded - With Glides | Yes | 42" | 7 91/128" | 40 13/16" | 4 37/128" | No | 15 127/128" | No | No | No | 54" |
| 24d 60w 42h - C Leg Extruded - With Glides | No | 24" | 42" | 60" | Yes | No | No | 24" | Haworth Jive Table Rectangle Legs - 24d 60w 42h - C Leg Extruded - With Glides | Yes | 42" | 7 91/128" | 40 13/16" | 4 37/128" | No | 15 127/128" | No | No | No | 60" |
| 24d 66w 42h - C Leg Extruded - With Glides | No | 24" | 42" | 66" | Yes | No | No | 24" | Haworth Jive Table Rectangle Legs - 24d 66w 42h - C Leg Extruded - With Glides | Yes | 42" | 7 91/128" | 40 13/16" | 4 37/128" | No | 15 127/128" | No | No | No | 66" |
| 24d 72w 42h - C Leg Extruded - With Glides | No | 24" | 42" | 72" | Yes | No | No | 24" | Haworth Jive Table Rectangle Legs - 24d 72w 42h - C Leg Extruded - With Glides | Yes | 42" | 7 91/128" | 40 13/16" | 4 37/128" | No | 15 127/128" | No | No | No | 72" |
| 30d 72w 42h - C Leg Extruded - With Glides | No | 30" | 42" | 72" | Yes | No | No | 30" | Haworth Jive Table Rectangle Legs - 30d 72w 42h - C Leg Extruded - With Glides | Yes | 42" | 7 91/128" | 40 13/16" | 7 37/128" | No | 21 127/128" | No | No | No | 72" |
| 24d 36w 29h - C Leg Round - With Casters | Yes | 24" | 29" | 36" | No | Yes | Yes | 24" | Haworth Jive Table Rectangle Legs - 24d 36w 29h - C Leg Round - With Casters | No | 29" | 8 53/64" | 27 13/16" | 3 11/64" | No | 15 127/128" | No | No | No | 36" |
| 24d 42w 29h - C Leg Round - With Casters | Yes | 24" | 29" | 42" | No | Yes | Yes | 24" | Haworth Jive Table Rectangle Legs - 24d 42w 29h - C Leg Round - With Casters | No | 29" | 8 53/64" | 27 13/16" | 3 11/64" | No | 15 127/128" | No | No | No | 42" |
| 24d 48w 29h - C Leg Round - With Casters | Yes | 24" | 29" | 48" | No | Yes | Yes | 24" | Haworth Jive Table Rectangle Legs - 24d 48w 29h - C Leg Round - With Casters | No | 29" | 8 53/64" | 27 13/16" | 3 11/64" | No | 15 127/128" | No | No | No | 48" |
| 24d 54w 29h - C Leg Round - With Casters | Yes | 24" | 29" | 54" | No | Yes | Yes | 24" | Haworth Jive Table Rectangle Legs - 24d 54w 29h - C Leg Round - With Casters | No | 29" | 8 53/64" | 27 13/16" | 3 11/64" | No | 15 127/128" | No | No | No | 54" |
| 24d 60w 29h - C Leg Round - With Casters | Yes | 24" | 29" | 60" | No | Yes | Yes | 24" | Haworth Jive Table Rectangle Legs - 24d 60w 29h - C Leg Round - With Casters | No | 29" | 8 53/64" | 27 13/16" | 3 11/64" | No | 15 127/128" | No | No | No | 60" |
| 24d 66w 29h - C Leg Round - With Casters | Yes | 24" | 29" | 66" | No | Yes | Yes | 24" | Haworth Jive Table Rectangle Legs - 24d 66w 29h - C Leg Round - With Casters | No | 29" | 8 53/64" | 27 13/16" | 3 11/64" | No | 15 127/128" | No | No | No | 66" |
| 24d 72w 29h - C Leg Round - With Casters | Yes | 24" | 29" | 72" | No | Yes | Yes | 24" | Haworth Jive Table Rectangle Legs - 24d 72w 29h - C Leg Round - With Casters | No | 29" | 8 53/64" | 27 13/16" | 3 11/64" | No | 15 127/128" | No | No | No | 72" |
| 30d 36w 29h - C Leg Round - With Casters | Yes | 30" | 29" | 36" | No | Yes | Yes | 30" | Haworth Jive Table Rectangle Legs - 30d 36w 29h - C Leg Round - With Casters | No | 29" | 8 53/64" | 27 13/16" | 6 11/64" | No | 21 127/128" | No | No | No | 36" |
| 30d 42w 29h - C Leg Round - With Casters | Yes | 30" | 29" | 42" | No | Yes | Yes | 30" | Haworth Jive Table Rectangle Legs - 30d 42w 29h - C Leg Round - With Casters | No | 29" | 8 53/64" | 27 13/16" | 6 11/64" | No | 21 127/128" | No | No | No | 42" |
| 30d 48w 29h - C Leg Round - With Casters | Yes | 30" | 29" | 48" | No | Yes | Yes | 30" | Haworth Jive Table Rectangle Legs - 30d 48w 29h - C Leg Round - With Casters | No | 29" | 8 53/64" | 27 13/16" | 6 11/64" | No | 21 127/128" | No | No | No | 48" |
| 30d 54w 29h - C Leg Round - With Casters | Yes | 30" | 29" | 54" | No | Yes | Yes | 30" | Haworth Jive Table Rectangle Legs - 30d 54w 29h - C Leg Round - With Casters | No | 29" | 8 53/64" | 27 13/16" | 6 11/64" | No | 21 127/128" | No | No | No | 54" |
| 30d 60w 29h - C Leg Round - With Casters | Yes | 30" | 29" | 60" | No | Yes | Yes | 30" | Haworth Jive Table Rectangle Legs - 30d 60w 29h - C Leg Round - With Casters | No | 29" | 8 53/64" | 27 13/16" | 6 11/64" | No | 21 127/128" | No | No | No | 60" |
| 30d 66w 29h - C Leg Round - With Casters | Yes | 30" | 29" | 66" | No | Yes | Yes | 30" | Haworth Jive Table Rectangle Legs - 30d 66w 29h - C Leg Round - With Casters | No | 29" | 8 53/64" | 27 13/16" | 6 11/64" | No | 21 127/128" | No | No | No | 66" |
| 30d 72w 29h - C Leg Round - With Casters | Yes | 30" | 29" | 72" | No | Yes | Yes | 30" | Haworth Jive Table Rectangle Legs - 30d 72w 29h - C Leg Round - With Casters | No | 29" | 8 53/64" | 27 13/16" | 6 11/64" | No | 21 127/128" | No | No | No | 72" |
| 24d 36w 29h - C Leg Round - With Glides | No | 24" | 29" | 36" | No | Yes | No | 24" | Haworth Jive Table Rectangle Legs - 24d 36w 29h - C Leg Round - With Glides | Yes | 29" | 8 53/64" | 27 13/16" | 3 11/64" | No | 15 127/128" | No | No | No | 36" |
| 24d 42w 29h - C Leg Round - With Glides | No | 24" | 29" | 42" | No | Yes | No | 24" | Haworth Jive Table Rectangle Legs - 24d 42w 29h - C Leg Round - With Glides | Yes | 29" | 8 53/64" | 27 13/16" | 3 11/64" | No | 15 127/128" | No | No | No | 42" |
| 24d 48w 29h - C Leg Round - With Glides | No | 24" | 29" | 48" | No | Yes | No | 24" | Haworth Jive Table Rectangle Legs - 24d 48w 29h - C Leg Round - With Glides | Yes | 29" | 8 53/64" | 27 13/16" | 3 11/64" | No | 15 127/128" | No | No | No | 48" |
| 24d 54w 29h - C Leg Round - With Glides | No | 24" | 29" | 54" | No | Yes | No | 24" | Haworth Jive Table Rectangle Legs - 24d 54w 29h - C Leg Round - With Glides | Yes | 29" | 8 53/64" | 27 13/16" | 3 11/64" | No | 15 127/128" | No | No | No | 54" |
| 24d 60w 29h - C Leg Round - With Glides | No | 24" | 29" | 60" | No | Yes | No | 24" | Haworth Jive Table Rectangle Legs - 24d 60w 29h - C Leg Round - With Glides | Yes | 29" | 8 53/64" | 27 13/16" | 3 11/64" | No | 15 127/128" | No | No | No | 60" |
| 24d 66w 29h - C Leg Round - With Glides | No | 24" | 29" | 66" | No | Yes | No | 24" | Haworth Jive Table Rectangle Legs - 24d 66w 29h - C Leg Round - With Glides | Yes | 29" | 8 53/64" | 27 13/16" | 3 11/64" | No | 15 127/128" | No | No | No | 66" |
| 24d 72w 29h - C Leg Round - With Glides | No | 24" | 29" | 72" | No | Yes | No | 24" | Haworth Jive Table Rectangle Legs - 24d 72w 29h - C Leg Round - With Glides | Yes | 29" | 8 53/64" | 27 13/16" | 3 11/64" | No | 15 127/128" | No | No | No | 72" |
| 30d 36w 29h - C Leg Round - With Glides | No | 30" | 29" | 36" | No | Yes | No | 30" | Haworth Jive Table Rectangle Legs - 30d 36w 29h - C Leg Round - With Glides | Yes | 29" | 8 53/64" | 27 13/16" | 6 11/64" | No | 21 127/128" | No | No | No | 36" |
| 30d 42w 29h - C Leg Round - With Glides | No | 30" | 29" | 42" | No | Yes | No | 30" | Haworth Jive Table Rectangle Legs - 30d 42w 29h - C Leg Round - With Glides | Yes | 29" | 8 53/64" | 27 13/16" | 6 11/64" | No | 21 127/128" | No | No | No | 42" |
| 30d 48w 29h - C Leg Round - With Glides | No | 30" | 29" | 48" | No | Yes | No | 30" | Haworth Jive Table Rectangle Legs - 30d 48w 29h - C Leg Round - With Glides | Yes | 29" | 8 53/64" | 27 13/16" | 6 11/64" | No | 21 127/128" | No | No | No | 48" |
| 30d 54w 29h - C Leg Round - With Glides | No | 30" | 29" | 54" | No | Yes | No | 30" | Haworth Jive Table Rectangle Legs - 30d 54w 29h - C Leg Round - With Glides | Yes | 29" | 8 53/64" | 27 13/16" | 6 11/64" | No | 21 127/128" | No | No | No | 54" |
| 30d 60w 29h - C Leg Round - With Glides | No | 30" | 29" | 60" | No | Yes | No | 30" | Haworth Jive Table Rectangle Legs - 30d 60w 29h - C Leg Round - With Glides | Yes | 29" | 8 53/64" | 27 13/16" | 6 11/64" | No | 21 127/128" | No | No | No | 60" |
| 30d 66w 29h - C Leg Round - With Glides | No | 30" | 29" | 66" | No | Yes | No | 30" | Haworth Jive Table Rectangle Legs - 30d 66w 29h - C Leg Round - With Glides | Yes | 29" | 8 53/64" | 27 13/16" | 6 11/64" | No | 21 127/128" | No | No | No | 66" |
| 30d 72w 29h - C Leg Round - With Glides | No | 30" | 29" | 72" | No | Yes | No | 30" | Haworth Jive Table Rectangle Legs - 30d 72w 29h - C Leg Round - With Glides | Yes | 29" | 8 53/64" | 27 13/16" | 6 11/64" | No | 21 127/128" | No | No | No | 72" |
| 24d 48w 42h - C Leg Round - With Glides | No | 24" | 42" | 48" | No | Yes | No | 24" | Haworth Jive Table Rectangle Legs - 24d 48w 42h - C Leg Round - With Glides | Yes | 42" | 8 53/64" | 40 13/16" | 3 11/64" | No | 15 127/128" | No | No | No | 48" |
| 24d 54w 42h - C Leg Round - With Glides | No | 24" | 42" | 54" | No | Yes | No | 24" | Haworth Jive Table Rectangle Legs - 24d 54w 42h - C Leg Round - With Glides | Yes | 42" | 8 53/64" | 40 13/16" | 3 11/64" | No | 15 127/128" | No | No | No | 54" |
| 24d 60w 42h - C Leg Round - With Glides | No | 24" | 42" | 60" | No | Yes | No | 24" | Haworth Jive Table Rectangle Legs - 24d 60w 42h - C Leg Round - With Glides | Yes | 42" | 8 53/64" | 40 13/16" | 3 11/64" | No | 15 127/128" | No | No | No | 60" |
| 24d 66w 42h - C Leg Round - With Glides | No | 24" | 42" | 66" | No | Yes | No | 24" | Haworth Jive Table Rectangle Legs - 24d 66w 42h - C Leg Round - With Glides | Yes | 42" | 8 53/64" | 40 13/16" | 3 11/64" | No | 15 127/128" | No | No | No | 66" |
| 24d 72w 42h - C Leg Round - With Glides | No | 24" | 42" | 72" | No | Yes | No | 24" | Haworth Jive Table Rectangle Legs - 24d 72w 42h - C Leg Round - With Glides | Yes | 42" | 8 53/64" | 40 13/16" | 3 11/64" | No | 15 127/128" | No | No | No | 72" |
| 30d 72w 42h - C Leg Round - With Glides | No | 30" | 42" | 72" | No | Yes | No | 30" | Haworth Jive Table Rectangle Legs - 30d 72w 42h - C Leg Round - With Glides | Yes | 42" | 8 53/64" | 40 13/16" | 6 11/64" | No | 21 127/128" | No | No | No | 72" |
| 18d 48w 29h - T Leg Extruded - With Glides | No | 18" | 29" | 48" | No | No | No | 18" | Haworth Jive Table Rectangle Legs - 18d 48w 29h - T Leg Extruded - With Glides | Yes | 29" | 7 91/128" | 27 13/16" | 1 37/128" | No | 9 127/128" | No | Yes | No | 48" |
| 18d 54w 29h - T Leg Extruded - With Glides | No | 18" | 29" | 54" | No | No | No | 18" | Haworth Jive Table Rectangle Legs - 18d 54w 29h - T Leg Extruded - With Glides | Yes | 29" | 7 91/128" | 27 13/16" | 1 37/128" | No | 9 127/128" | No | Yes | No | 54" |
| 18d 60w 29h - T Leg Extruded - With Glides | No | 18" | 29" | 60" | No | No | No | 18" | Haworth Jive Table Rectangle Legs - 18d 60w 29h - T Leg Extruded - With Glides | Yes | 29" | 7 91/128" | 27 13/16" | 1 37/128" | No | 9 127/128" | No | Yes | No | 60" |
| 18d 66w 29h - T Leg Extruded - With Glides | No | 18" | 29" | 66" | No | No | No | 18" | Haworth Jive Table Rectangle Legs - 18d 66w 29h - T Leg Extruded - With Glides | Yes | 29" | 7 91/128" | 27 13/16" | 1 37/128" | No | 9 127/128" | No | Yes | No | 66" |
| 18d 72w 29h - T Leg Extruded - With Glides | No | 18" | 29" | 72" | No | No | No | 18" | Haworth Jive Table Rectangle Legs - 18d 72w 29h - T Leg Extruded - With Glides | Yes | 29" | 7 91/128" | 27 13/16" | 1 37/128" | No | 9 127/128" | No | Yes | No | 72" |
| 24d 36w 29h - T Leg Extruded - With Glides | No | 24" | 29" | 36" | No | No | No | 24" | Haworth Jive Table Rectangle Legs - 24d 36w 29h - T Leg Extruded - With Glides | Yes | 29" | 7 91/128" | 27 13/16" | 4 37/128" | No | 15 127/128" | No | Yes | No | 36" |
| 24d 42w 29h - T Leg Extruded - With Glides | No | 24" | 29" | 42" | No | No | No | 24" | Haworth Jive Table Rectangle Legs - 24d 42w 29h - T Leg Extruded - With Glides | Yes | 29" | 7 91/128" | 27 13/16" | 4 37/128" | No | 15 127/128" | No | Yes | No | 42" |
| 24d 48w 29h - T Leg Extruded - With Glides | No | 24" | 29" | 48" | No | No | No | 24" | Haworth Jive Table Rectangle Legs - 24d 48w 29h - T Leg Extruded - With Glides | Yes | 29" | 7 91/128" | 27 13/16" | 4 37/128" | No | 15 127/128" | No | Yes | No | 48" |
| 24d 54w 29h - T Leg Extruded - With Glides | No | 24" | 29" | 54" | No | No | No | 24" | Haworth Jive Table Rectangle Legs - 24d 54w 29h - T Leg Extruded - With Glides | Yes | 29" | 7 91/128" | 27 13/16" | 4 37/128" | No | 15 127/128" | No | Yes | No | 54" |
| 24d 60w 29h - T Leg Extruded - With Glides | No | 24" | 29" | 60" | No | No | No | 24" | Haworth Jive Table Rectangle Legs - 24d 60w 29h - T Leg Extruded - With Glides | Yes | 29" | 7 91/128" | 27 13/16" | 4 37/128" | No | 15 127/128" | No | Yes | No | 60" |
| 24d 66w 29h - T Leg Extruded - With Glides | No | 24" | 29" | 66" | No | No | No | 24" | Haworth Jive Table Rectangle Legs - 24d 66w 29h - T Leg Extruded - With Glides | Yes | 29" | 7 91/128" | 27 13/16" | 4 37/128" | No | 15 127/128" | No | Yes | No | 66" |
| 24d 72w 29h - T Leg Extruded - With Glides | No | 24" | 29" | 72" | No | No | No | 24" | Haworth Jive Table Rectangle Legs - 24d 72w 29h - T Leg Extruded - With Glides | Yes | 29" | 7 91/128" | 27 13/16" | 4 37/128" | No | 15 127/128" | No | Yes | No | 72" |
| 30d 36w 29h - T Leg Extruded - With Glides | No | 30" | 29" | 36" | No | No | No | 30" | Haworth Jive Table Rectangle Legs - 30d 36w 29h - T Leg Extruded - With Glides | Yes | 29" | 7 91/128" | 27 13/16" | 7 37/128" | No | 21 127/128" | No | Yes | No | 36" |
| 30d 42w 29h - T Leg Extruded - With Glides | No | 30" | 29" | 42" | No | No | No | 30" | Haworth Jive Table Rectangle Legs - 30d 42w 29h - T Leg Extruded - With Glides | Yes | 29" | 7 91/128" | 27 13/16" | 7 37/128" | No | 21 127/128" | No | Yes | No | 42" |
| 30d 48w 29h - T Leg Extruded - With Glides | No | 30" | 29" | 48" | No | No | No | 30" | Haworth Jive Table Rectangle Legs - 30d 48w 29h - T Leg Extruded - With Glides | Yes | 29" | 7 91/128" | 27 13/16" | 7 37/128" | No | 21 127/128" | No | Yes | No | 48" |
| 30d 54w 29h - T Leg Extruded - With Glides | No | 30" | 29" | 54" | No | No | No | 30" | Haworth Jive Table Rectangle Legs - 30d 54w 29h - T Leg Extruded - With Glides | Yes | 29" | 7 91/128" | 27 13/16" | 7 37/128" | No | 21 127/128" | No | Yes | No | 54" |
| 30d 60w 29h - T Leg Extruded - With Glides | No | 30" | 29" | 60" | No | No | No | 30" | Haworth Jive Table Rectangle Legs - 30d 60w 29h - T Leg Extruded - With Glides | Yes | 29" | 7 91/128" | 27 13/16" | 7 37/128" | No | 21 127/128" | No | Yes | No | 60" |
| 30d 66w 29h - T Leg Extruded - With Glides | No | 30" | 29" | 66" | No | No | No | 30" | Haworth Jive Table Rectangle Legs - 30d 66w 29h - T Leg Extruded - With Glides | Yes | 29" | 7 91/128" | 27 13/16" | 7 37/128" | No | 21 127/128" | No | Yes | No | 66" |
| 30d 72w 29h - T Leg Extruded - With Glides | No | 30" | 29" | 72" | No | No | No | 30" | Haworth Jive Table Rectangle Legs - 30d 72w 29h - T Leg Extruded - With Glides | Yes | 29" | 7 91/128" | 27 13/16" | 7 37/128" | No | 21 127/128" | No | Yes | No | 72" |
| 36d 60w 29h - T Leg Extruded - With Glides | No | 36" | 29" | 60" | No | No | No | 36" | Haworth Jive Table Rectangle Legs - 36d 60w 29h - T Leg Extruded - With Glides | Yes | 29" | 7 91/128" | 27 13/16" | 10 37/128" | No | 27 127/128" | No | Yes | No | 60" |
| 36d 66w 29h - T Leg Extruded - With Glides | No | 36" | 29" | 66" | No | No | No | 36" | Haworth Jive Table Rectangle Legs - 36d 66w 29h - T Leg Extruded - With Glides | Yes | 29" | 7 91/128" | 27 13/16" | 10 37/128" | No | 27 127/128" | No | Yes | No | 66" |
| 36d 72w 29h - T Leg Extruded - With Glides | No | 36" | 29" | 72" | No | No | No | 36" | Haworth Jive Table Rectangle Legs - 36d 72w 29h - T Leg Extruded - With Glides | Yes | 29" | 7 91/128" | 27 13/16" | 10 37/128" | No | 27 127/128" | No | Yes | No | 72" |
| 24d 36w 36h - T Leg Extruded - With Glides | No | 24" | 36" | 36" | No | No | No | 24" | Haworth Jive Table Rectangle Legs - 24d 36w 36h - T Leg Extruded - With Glides | Yes | 36" | 7 91/128" | 34 13/16" | 4 37/128" | No | 15 127/128" | No | Yes | No | 36" |
| 24d 42w 36h - T Leg Extruded - With Glides | No | 24" | 36" | 42" | No | No | No | 24" | Haworth Jive Table Rectangle Legs - 24d 42w 36h - T Leg Extruded - With Glides | Yes | 36" | 7 91/128" | 34 13/16" | 4 37/128" | No | 15 127/128" | No | Yes | No | 42" |
| 24d 48w 36h - T Leg Extruded - With Glides | No | 24" | 36" | 48" | No | No | No | 24" | Haworth Jive Table Rectangle Legs - 24d 48w 36h - T Leg Extruded - With Glides | Yes | 36" | 7 91/128" | 34 13/16" | 4 37/128" | No | 15 127/128" | No | Yes | No | 48" |
| 24d 54w 36h - T Leg Extruded - With Glides | No | 24" | 36" | 54" | No | No | No | 24" | Haworth Jive Table Rectangle Legs - 24d 54w 36h - T Leg Extruded - With Glides | Yes | 36" | 7 91/128" | 34 13/16" | 4 37/128" | No | 15 127/128" | No | Yes | No | 54" |
| 24d 60w 36h - T Leg Extruded - With Glides | No | 24" | 36" | 60" | No | No | No | 24" | Haworth Jive Table Rectangle Legs - 24d 60w 36h - T Leg Extruded - With Glides | Yes | 36" | 7 91/128" | 34 13/16" | 4 37/128" | No | 15 127/128" | No | Yes | No | 60" |
| 24d 66w 36h - T Leg Extruded - With Glides | No | 24" | 36" | 66" | No | No | No | 24" | Haworth Jive Table Rectangle Legs - 24d 66w 36h - T Leg Extruded - With Glides | Yes | 36" | 7 91/128" | 34 13/16" | 4 37/128" | No | 15 127/128" | No | Yes | No | 66" |
| 24d 72w 36h - T Leg Extruded - With Glides | No | 24" | 36" | 72" | No | No | No | 24" | Haworth Jive Table Rectangle Legs - 24d 72w 36h - T Leg Extruded - With Glides | Yes | 36" | 7 91/128" | 34 13/16" | 4 37/128" | No | 15 127/128" | No | Yes | No | 72" |
| 30d 36w 36h - T Leg Extruded - With Glides | No | 30" | 36" | 36" | No | No | No | 30" | Haworth Jive Table Rectangle Legs - 30d 36w 36h - T Leg Extruded - With Glides | Yes | 36" | 7 91/128" | 34 13/16" | 7 37/128" | No | 21 127/128" | No | Yes | No | 36" |
| 30d 42w 36h - T Leg Extruded - With Glides | No | 30" | 36" | 42" | No | No | No | 30" | Haworth Jive Table Rectangle Legs - 30d 42w 36h - T Leg Extruded - With Glides | Yes | 36" | 7 91/128" | 34 13/16" | 7 37/128" | No | 21 127/128" | No | Yes | No | 42" |
| 30d 48w 36h - T Leg Extruded - With Glides | No | 30" | 36" | 48" | No | No | No | 30" | Haworth Jive Table Rectangle Legs - 30d 48w 36h - T Leg Extruded - With Glides | Yes | 36" | 7 91/128" | 34 13/16" | 7 37/128" | No | 21 127/128" | No | Yes | No | 48" |
| 30d 54w 36h - T Leg Extruded - With Glides | No | 30" | 36" | 54" | No | No | No | 30" | Haworth Jive Table Rectangle Legs - 30d 54w 36h - T Leg Extruded - With Glides | Yes | 36" | 7 91/128" | 34 13/16" | 7 37/128" | No | 21 127/128" | No | Yes | No | 54" |
| 30d 60w 36h - T Leg Extruded - With Glides | No | 30" | 36" | 60" | No | No | No | 30" | Haworth Jive Table Rectangle Legs - 30d 60w 36h - T Leg Extruded - With Glides | Yes | 36" | 7 91/128" | 34 13/16" | 7 37/128" | No | 21 127/128" | No | Yes | No | 60" |
| 30d 66w 36h - T Leg Extruded - With Glides | No | 30" | 36" | 66" | No | No | No | 30" | Haworth Jive Table Rectangle Legs - 30d 66w 36h - T Leg Extruded - With Glides | Yes | 36" | 7 91/128" | 34 13/16" | 7 37/128" | No | 21 127/128" | No | Yes | No | 66" |
| 30d 72w 36h - T Leg Extruded - With Glides | No | 30" | 36" | 72" | No | No | No | 30" | Haworth Jive Table Rectangle Legs - 30d 72w 36h - T Leg Extruded - With Glides | Yes | 36" | 7 91/128" | 34 13/16" | 7 37/128" | No | 21 127/128" | No | Yes | No | 72" |
| 36d 66w 36h - T Leg Extruded - With Glides | No | 36" | 36" | 66" | No | No | No | 36" | Haworth Jive Table Rectangle Legs - 36d 66w 36h - T Leg Extruded - With Glides | Yes | 36" | 7 91/128" | 34 13/16" | 10 37/128" | No | 27 127/128" | No | Yes | No | 66" |
| 36d 72w 36h - T Leg Extruded - With Glides | No | 36" | 36" | 72" | No | No | No | 36" | Haworth Jive Table Rectangle Legs - 36d 72w 36h - T Leg Extruded - With Glides | Yes | 36" | 7 91/128" | 34 13/16" | 10 37/128" | No | 27 127/128" | No | Yes | No | 72" |
| 24d 36w 42h - T Leg Extruded - With Glides | No | 24" | 42" | 36" | No | No | No | 24" | Haworth Jive Table Rectangle Legs - 24d 36w 42h - T Leg Extruded - With Glides | Yes | 42" | 7 91/128" | 40 13/16" | 4 37/128" | No | 15 127/128" | No | Yes | No | 36" |
| 24d 42w 42h - T Leg Extruded - With Glides | No | 24" | 42" | 42" | No | No | No | 24" | Haworth Jive Table Rectangle Legs - 24d 42w 42h - T Leg Extruded - With Glides | Yes | 42" | 7 91/128" | 40 13/16" | 4 37/128" | No | 15 127/128" | No | Yes | No | 42" |
| 24d 48w 42h - T Leg Extruded - With Glides | No | 24" | 42" | 48" | No | No | No | 24" | Haworth Jive Table Rectangle Legs - 24d 48w 42h - T Leg Extruded - With Glides | Yes | 42" | 7 91/128" | 40 13/16" | 4 37/128" | No | 15 127/128" | No | Yes | No | 48" |
| 24d 54w 42h - T Leg Extruded - With Glides | No | 24" | 42" | 54" | No | No | No | 24" | Haworth Jive Table Rectangle Legs - 24d 54w 42h - T Leg Extruded - With Glides | Yes | 42" | 7 91/128" | 40 13/16" | 4 37/128" | No | 15 127/128" | No | Yes | No | 54" |
| 24d 60w 42h - T Leg Extruded - With Glides | No | 24" | 42" | 60" | No | No | No | 24" | Haworth Jive Table Rectangle Legs - 24d 60w 42h - T Leg Extruded - With Glides | Yes | 42" | 7 91/128" | 40 13/16" | 4 37/128" | No | 15 127/128" | No | Yes | No | 60" |
| 24d 66w 42h - T Leg Extruded - With Glides | No | 24" | 42" | 66" | No | No | No | 24" | Haworth Jive Table Rectangle Legs - 24d 66w 42h - T Leg Extruded - With Glides | Yes | 42" | 7 91/128" | 40 13/16" | 4 37/128" | No | 15 127/128" | No | Yes | No | 66" |
| 24d 72w 42h - T Leg Extruded - With Glides | No | 24" | 42" | 72" | No | No | No | 24" | Haworth Jive Table Rectangle Legs - 24d 72w 42h - T Leg Extruded - With Glides | Yes | 42" | 7 91/128" | 40 13/16" | 4 37/128" | No | 15 127/128" | No | Yes | No | 72" |
| 30d 36w 42h - T Leg Extruded - With Glides | No | 30" | 42" | 36" | No | No | No | 30" | Haworth Jive Table Rectangle Legs - 30d 36w 42h - T Leg Extruded - With Glides | Yes | 42" | 7 91/128" | 40 13/16" | 7 37/128" | No | 21 127/128" | No | Yes | No | 36" |
| 30d 42w 42h - T Leg Extruded - With Glides | No | 30" | 42" | 42" | No | No | No | 30" | Haworth Jive Table Rectangle Legs - 30d 42w 42h - T Leg Extruded - With Glides | Yes | 42" | 7 91/128" | 40 13/16" | 7 37/128" | No | 21 127/128" | No | Yes | No | 42" |
| 30d 48w 42h - T Leg Extruded - With Glides | No | 30" | 42" | 48" | No | No | No | 30" | Haworth Jive Table Rectangle Legs - 30d 48w 42h - T Leg Extruded - With Glides | Yes | 42" | 7 91/128" | 40 13/16" | 7 37/128" | No | 21 127/128" | No | Yes | No | 48" |
| 30d 54w 42h - T Leg Extruded - With Glides | No | 30" | 42" | 54" | No | No | No | 30" | Haworth Jive Table Rectangle Legs - 30d 54w 42h - T Leg Extruded - With Glides | Yes | 42" | 7 91/128" | 40 13/16" | 7 37/128" | No | 21 127/128" | No | Yes | No | 54" |
| 30d 60w 42h - T Leg Extruded - With Glides | No | 30" | 42" | 60" | No | No | No | 30" | Haworth Jive Table Rectangle Legs - 30d 60w 42h - T Leg Extruded - With Glides | Yes | 42" | 7 91/128" | 40 13/16" | 7 37/128" | No | 21 127/128" | No | Yes | No | 60" |
| 30d 66w 42h - T Leg Extruded - With Glides | No | 30" | 42" | 66" | No | No | No | 30" | Haworth Jive Table Rectangle Legs - 30d 66w 42h - T Leg Extruded - With Glides | Yes | 42" | 7 91/128" | 40 13/16" | 7 37/128" | No | 21 127/128" | No | Yes | No | 66" |
| 30d 72w 42h - T Leg Extruded - With Glides | No | 30" | 42" | 72" | No | No | No | 30" | Haworth Jive Table Rectangle Legs - 30d 72w 42h - T Leg Extruded - With Glides | Yes | 42" | 7 91/128" | 40 13/16" | 7 37/128" | No | 21 127/128" | No | Yes | No | 72" |
| 36d 66w 42h - T Leg Extruded - With Glides | No | 36" | 42" | 66" | No | No | No | 36" | Haworth Jive Table Rectangle Legs - 36d 66w 42h - T Leg Extruded - With Glides | Yes | 42" | 7 91/128" | 40 13/16" | 10 37/128" | No | 27 127/128" | No | Yes | No | 66" |
| 36d 72w 42h - T Leg Extruded - With Glides | No | 36" | 42" | 72" | No | No | No | 36" | Haworth Jive Table Rectangle Legs - 36d 72w 42h - T Leg Extruded - With Glides | Yes | 42" | 7 91/128" | 40 13/16" | 10 37/128" | No | 27 127/128" | No | Yes | No | 72" |
| 18d 48w 29h - T Leg Extruded - With Casters | Yes | 18" | 29" | 48" | No | No | Yes | 18" | Haworth Jive Table Rectangle Legs - 18d 48w 29h - T Leg Extruded - With Casters | No | 29" | 7 91/128" | 27 13/16" | 1 37/128" | No | 9 127/128" | No | Yes | No | 48" |
| 18d 54w 29h - T Leg Extruded - With Casters | Yes | 18" | 29" | 54" | No | No | Yes | 18" | Haworth Jive Table Rectangle Legs - 18d 54w 29h - T Leg Extruded - With Casters | No | 29" | 7 91/128" | 27 13/16" | 1 37/128" | No | 9 127/128" | No | Yes | No | 54" |
| 18d 60w 29h - T Leg Extruded - With Casters | Yes | 18" | 29" | 60" | No | No | Yes | 18" | Haworth Jive Table Rectangle Legs - 18d 60w 29h - T Leg Extruded - With Casters | No | 29" | 7 91/128" | 27 13/16" | 1 37/128" | No | 9 127/128" | No | Yes | No | 60" |
| 18d 66w 29h - T Leg Extruded - With Casters | Yes | 18" | 29" | 66" | No | No | Yes | 18" | Haworth Jive Table Rectangle Legs - 18d 66w 29h - T Leg Extruded - With Casters | No | 29" | 7 91/128" | 27 13/16" | 1 37/128" | No | 9 127/128" | No | Yes | No | 66" |
| 18d 72w 29h - T Leg Extruded - With Casters | Yes | 18" | 29" | 72" | No | No | Yes | 18" | Haworth Jive Table Rectangle Legs - 18d 72w 29h - T Leg Extruded - With Casters | No | 29" | 7 91/128" | 27 13/16" | 1 37/128" | No | 9 127/128" | No | Yes | No | 72" |
| 24d 36w 29h - T Leg Extruded - With Casters | Yes | 24" | 29" | 36" | No | No | Yes | 24" | Haworth Jive Table Rectangle Legs - 24d 36w 29h - T Leg Extruded - With Casters | No | 29" | 7 91/128" | 27 13/16" | 4 37/128" | No | 15 127/128" | No | Yes | No | 36" |
| 24d 42w 29h - T Leg Extruded - With Casters | Yes | 24" | 29" | 42" | No | No | Yes | 24" | Haworth Jive Table Rectangle Legs - 24d 42w 29h - T Leg Extruded - With Casters | No | 29" | 7 91/128" | 27 13/16" | 4 37/128" | No | 15 127/128" | No | Yes | No | 42" |
| 24d 48w 29h - T Leg Extruded - With Casters | Yes | 24" | 29" | 48" | No | No | Yes | 24" | Haworth Jive Table Rectangle Legs - 24d 48w 29h - T Leg Extruded - With Casters | No | 29" | 7 91/128" | 27 13/16" | 4 37/128" | No | 15 127/128" | No | Yes | No | 48" |
| 24d 54w 29h - T Leg Extruded - With Casters | Yes | 24" | 29" | 54" | No | No | Yes | 24" | Haworth Jive Table Rectangle Legs - 24d 54w 29h - T Leg Extruded - With Casters | No | 29" | 7 91/128" | 27 13/16" | 4 37/128" | No | 15 127/128" | No | Yes | No | 54" |
| 24d 60w 29h - T Leg Extruded - With Casters | Yes | 24" | 29" | 60" | No | No | Yes | 24" | Haworth Jive Table Rectangle Legs - 24d 60w 29h - T Leg Extruded - With Casters | No | 29" | 7 91/128" | 27 13/16" | 4 37/128" | No | 15 127/128" | No | Yes | No | 60" |
| 24d 66w 29h - T Leg Extruded - With Casters | Yes | 24" | 29" | 66" | No | No | Yes | 24" | Haworth Jive Table Rectangle Legs - 24d 66w 29h - T Leg Extruded - With Casters | No | 29" | 7 91/128" | 27 13/16" | 4 37/128" | No | 15 127/128" | No | Yes | No | 66" |
| 24d 72w 29h - T Leg Extruded - With Casters | Yes | 24" | 29" | 72" | No | No | Yes | 24" | Haworth Jive Table Rectangle Legs - 24d 72w 29h - T Leg Extruded - With Casters | No | 29" | 7 91/128" | 27 13/16" | 4 37/128" | No | 15 127/128" | No | Yes | No | 72" |
| 30d 36w 29h - T Leg Extruded - With Casters | Yes | 30" | 29" | 36" | No | No | Yes | 30" | Haworth Jive Table Rectangle Legs - 30d 36w 29h - T Leg Extruded - With Casters | No | 29" | 7 91/128" | 27 13/16" | 7 37/128" | No | 21 127/128" | No | Yes | No | 36" |
| 30d 42w 29h - T Leg Extruded - With Casters | Yes | 30" | 29" | 42" | No | No | Yes | 30" | Haworth Jive Table Rectangle Legs - 30d 42w 29h - T Leg Extruded - With Casters | No | 29" | 7 91/128" | 27 13/16" | 7 37/128" | No | 21 127/128" | No | Yes | No | 42" |
| 30d 48w 29h - T Leg Extruded - With Casters | Yes | 30" | 29" | 48" | No | No | Yes | 30" | Haworth Jive Table Rectangle Legs - 30d 48w 29h - T Leg Extruded - With Casters | No | 29" | 7 91/128" | 27 13/16" | 7 37/128" | No | 21 127/128" | No | Yes | No | 48" |
| 30d 54w 29h - T Leg Extruded - With Casters | Yes | 30" | 29" | 54" | No | No | Yes | 30" | Haworth Jive Table Rectangle Legs - 30d 54w 29h - T Leg Extruded - With Casters | No | 29" | 7 91/128" | 27 13/16" | 7 37/128" | No | 21 127/128" | No | Yes | No | 54" |
| 30d 60w 29h - T Leg Extruded - With Casters | Yes | 30" | 29" | 60" | No | No | Yes | 30" | Haworth Jive Table Rectangle Legs - 30d 60w 29h - T Leg Extruded - With Casters | No | 29" | 7 91/128" | 27 13/16" | 7 37/128" | No | 21 127/128" | No | Yes | No | 60" |
| 30d 66w 29h - T Leg Extruded - With Casters | Yes | 30" | 29" | 66" | No | No | Yes | 30" | Haworth Jive Table Rectangle Legs - 30d 66w 29h - T Leg Extruded - With Casters | No | 29" | 7 91/128" | 27 13/16" | 7 37/128" | No | 21 127/128" | No | Yes | No | 66" |
| 30d 72w 29h - T Leg Extruded - With Casters | Yes | 30" | 29" | 72" | No | No | Yes | 30" | Haworth Jive Table Rectangle Legs - 30d 72w 29h - T Leg Extruded - With Casters | No | 29" | 7 91/128" | 27 13/16" | 7 37/128" | No | 21 127/128" | No | Yes | No | 72" |
| 36d 60w 29h - T Leg Extruded - With Casters | Yes | 36" | 29" | 60" | No | No | Yes | 36" | Haworth Jive Table Rectangle Legs - 36d 60w 29h - T Leg Extruded - With Casters | No | 29" | 7 91/128" | 27 13/16" | 10 37/128" | No | 27 127/128" | No | Yes | No | 60" |
| 36d 66w 29h - T Leg Extruded - With Casters | Yes | 36" | 29" | 66" | No | No | Yes | 36" | Haworth Jive Table Rectangle Legs - 36d 66w 29h - T Leg Extruded - With Casters | No | 29" | 7 91/128" | 27 13/16" | 10 37/128" | No | 27 127/128" | No | Yes | No | 66" |
| 36d 72w 29h - T Leg Extruded - With Casters | Yes | 36" | 29" | 72" | No | No | Yes | 36" | Haworth Jive Table Rectangle Legs - 36d 72w 29h - T Leg Extruded - With Casters | No | 29" | 7 91/128" | 27 13/16" | 10 37/128" | No | 27 127/128" | No | Yes | No | 72" |
| 36d 66w 29h - T Leg Round - With Glides | No | 36" | 29" | 66" | No | No | No | 36" | Haworth Jive Table Rectangle Legs - 36d 66w 29h - T Leg Round - With Glides | Yes | 29" | 8 53/64" | 27 13/16" | 9 11/64" | No | 27 127/128" | No | No | Yes | 66" |
| 36d 72w 29h - T Leg Round - With Glides | No | 36" | 29" | 72" | No | No | No | 36" | Haworth Jive Table Rectangle Legs - 36d 72w 29h - T Leg Round - With Glides | Yes | 29" | 8 53/64" | 27 13/16" | 9 11/64" | No | 27 127/128" | No | No | Yes | 72" |
| 36d 84w 29h - T Leg Round - With Glides | No | 36" | 29" | 84" | No | No | No | 36" | Haworth Jive Table Rectangle Legs - 36d 84w 29h - T Leg Round - With Glides | Yes | 29" | 8 53/64" | 27 13/16" | 9 11/64" | No | 27 127/128" | No | No | Yes | 84" |
| 36d 66w 36h - T Leg Round - With Glides | No | 36" | 36" | 66" | No | No | No | 36" | Haworth Jive Table Rectangle Legs - 36d 66w 36h - T Leg Round - With Glides | Yes | 36" | 8 53/64" | 34 13/16" | 9 11/64" | No | 27 127/128" | No | No | Yes | 66" |
| 36d 72w 36h - T Leg Round - With Glides | No | 36" | 36" | 72" | No | No | No | 36" | Haworth Jive Table Rectangle Legs - 36d 72w 36h - T Leg Round - With Glides | Yes | 36" | 8 53/64" | 34 13/16" | 9 11/64" | No | 27 127/128" | No | No | Yes | 72" |
| 36d 84w 36h - T Leg Round - With Glides | No | 36" | 36" | 84" | No | No | No | 36" | Haworth Jive Table Rectangle Legs - 36d 84w 36h - T Leg Round - With Glides | Yes | 36" | 8 53/64" | 34 13/16" | 9 11/64" | No | 27 127/128" | No | No | Yes | 84" |
| 36d 66w 42h - T Leg Round - With Glides | No | 36" | 42" | 66" | No | No | No | 36" | Haworth Jive Table Rectangle Legs - 36d 66w 42h - T Leg Round - With Glides | Yes | 42" | 8 53/64" | 40 13/16" | 9 11/64" | No | 27 127/128" | No | No | Yes | 66" |
| 36d 72w 42h - T Leg Round - With Glides | No | 36" | 42" | 72" | No | No | No | 36" | Haworth Jive Table Rectangle Legs - 36d 72w 42h - T Leg Round - With Glides | Yes | 42" | 8 53/64" | 40 13/16" | 9 11/64" | No | 27 127/128" | No | No | Yes | 72" |
| 36d 84w 42h - T Leg Round - With Glides | No | 36" | 42" | 84" | No | No | No | 36" | Haworth Jive Table Rectangle Legs - 36d 84w 42h - T Leg Round - With Glides | Yes | 42" | 8 53/64" | 40 13/16" | 9 11/64" | No | 27 127/128" | No | No | Yes | 84" |
| 36d 66w 29h - T Leg Round - With Casters | Yes | 36" | 29" | 66" | No | No | Yes | 36" | Haworth Jive Table Rectangle Legs - 36d 66w 29h - T Leg Round - With Casters | No | 29" | 8 53/64" | 27 13/16" | 9 11/64" | No | 27 127/128" | No | No | Yes | 66" |
| 36d 72w 29h - T Leg Round - With Casters | Yes | 36" | 29" | 72" | No | No | Yes | 36" | Haworth Jive Table Rectangle Legs - 36d 72w 29h - T Leg Round - With Casters | No | 29" | 8 53/64" | 27 13/16" | 9 11/64" | No | 27 127/128" | No | No | Yes | 72" |
| 36d 84w 29h - T Leg Round - With Casters | Yes | 36" | 29" | 84" | No | No | Yes | 36" | Haworth Jive Table Rectangle Legs - 36d 84w 29h - T Leg Round - With Casters | No | 29" | 8 53/64" | 27 13/16" | 9 11/64" | No | 27 127/128" | No | No | Yes | 84" |

## geometry (parser evidence)
native form markers: Sweep x32
no freeform markers — native parametric forms only
